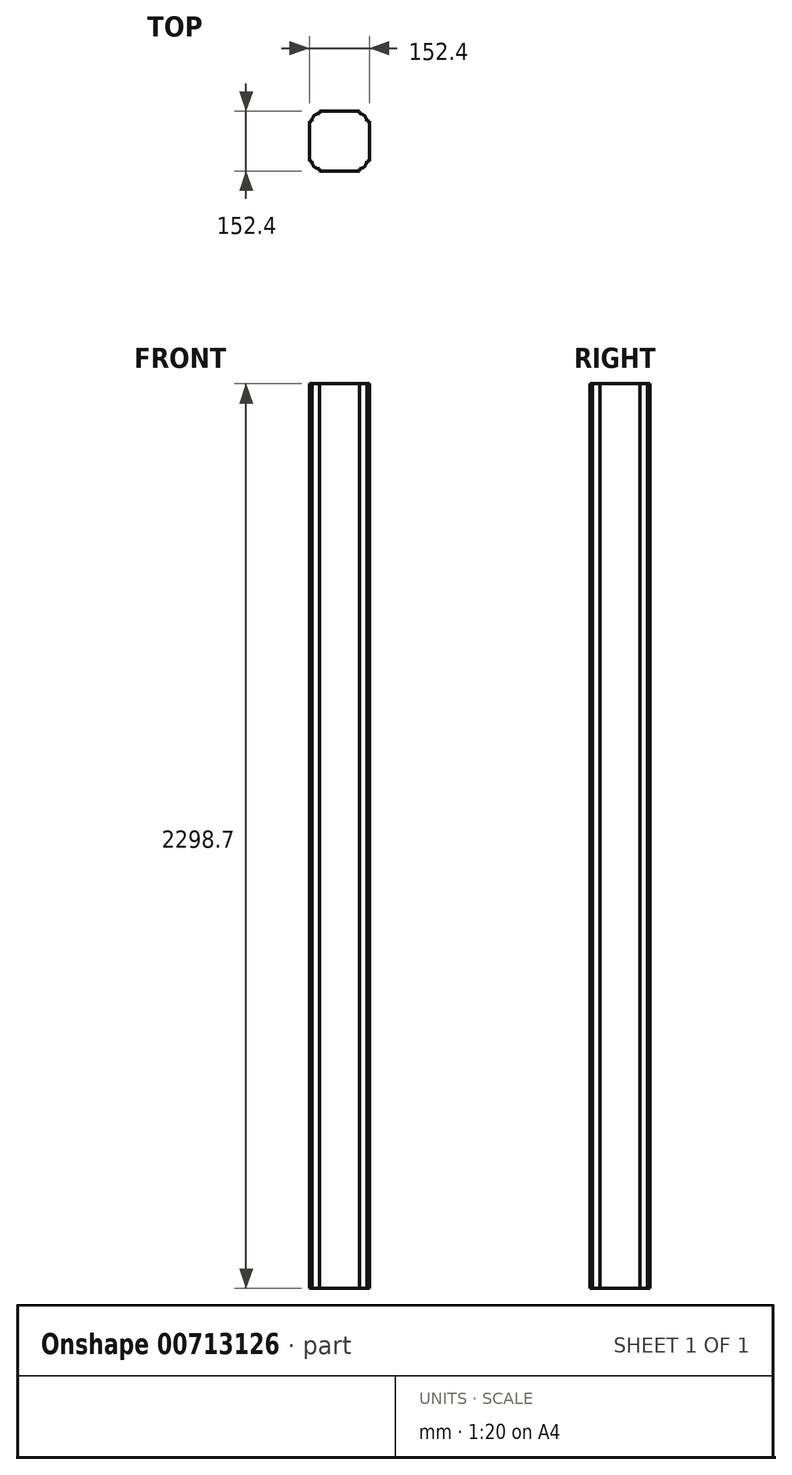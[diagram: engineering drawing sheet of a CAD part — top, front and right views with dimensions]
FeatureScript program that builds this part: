
annotation { "Feature Type Name" : "Feature", "Feature Type Description" : "" }
export const myFeature = defineFeature(function(context is Context, id is Id, definition is map)
    precondition{}
    {
        {
            var Q0;
            Q0=qCreatedBy(makeId("Top.planeOp"),FACE);
            var sketch = newSketch(context, id + "F0", { "sketchPlane" : qUnion([Q0])});
            skLineSegment(sketch, "E0.bottom", {"start": v(50.8, 0) * mm, "end": v(-50.8, 0) * mm});
            skLineSegment(sketch, "E0.top", {"start": v(50.8, 152.4) * mm, "end": v(-50.8, 152.4) * mm});
            skLineSegment(sketch, "E0.left", {"start": v(76.2, 25.4) * mm, "end": v(76.2, 127) * mm});
            skLineSegment(sketch, "E0.right", {"start": v(-76.2, 25.4) * mm, "end": v(-76.2, 127) * mm});
            skPoint(sketch, "E0.middle", {"position": v(0, 76.2) * mm});
            skLineSegment(sketch, "E1", {"start": v(-50.8, 152.4) * mm, "end": v(-50.8, 146.05) * mm});
            skLineSegment(sketch, "E2", {"start": v(-76.2, 152.4) * mm, "end": v(76.2, 0) * mm, "construction": true});
            skLineSegment(sketch, "E3", {"start": v(76.2, 152.4) * mm, "end": v(-76.2, 0) * mm, "construction": true});
            skLineSegment(sketch, "E4", {"start": v(0, 152.4) * mm, "end": v(0, 0) * mm, "construction": true});
            skLineSegment(sketch, "E5", {"start": v(-76.2, 76.2) * mm, "end": v(76.2, 76.2) * mm, "construction": true});
            skLineSegment(sketch, "E6.MirrorCS", {"start": v(-76.2, 127) * mm, "end": v(-69.85, 127) * mm});
            skArc(sketch, "E7", {"start": v(-50.8, 146.05) * mm, "mid": v(-64.27, 140.47) * mm, "end": v(-69.85, 127) * mm});
            skLineSegment(sketch, "E8.MirrorCS", {"start": v(50.8, 152.4) * mm, "end": v(50.8, 146.05) * mm});
            skLineSegment(sketch, "E9.MirrorCS", {"start": v(76.2, 127) * mm, "end": v(69.85, 127) * mm});
            skArc(sketch, "E10.MirrorCS", {"start": v(50.8, 146.05) * mm, "mid": v(64.27, 140.47) * mm, "end": v(69.85, 127) * mm});
            skLineSegment(sketch, "E11.MirrorCS", {"start": v(-50.8, 152.4) * mm, "end": v(50.8, 152.4) * mm});
            skLineSegment(sketch, "E12.MirrorCS", {"start": v(-76.2, 25.4) * mm, "end": v(-69.85, 25.4) * mm});
            skLineSegment(sketch, "E13.MirrorCS", {"start": v(50.8, 0) * mm, "end": v(50.8, 6.35) * mm});
            skLineSegment(sketch, "E14.MirrorCS", {"start": v(-50.8, 0) * mm, "end": v(-50.8, 6.35) * mm});
            skLineSegment(sketch, "E15.MirrorCS", {"start": v(76.2, 25.4) * mm, "end": v(69.85, 25.4) * mm});
            skArc(sketch, "E16.MirrorCS", {"start": v(-50.8, 6.35) * mm, "mid": v(-64.27, 11.93) * mm, "end": v(-69.85, 25.4) * mm});
            skArc(sketch, "E17.MirrorCS", {"start": v(50.8, 6.35) * mm, "mid": v(64.27, 11.93) * mm, "end": v(69.85, 25.4) * mm});
            skLineSegment(sketch, "E18.MirrorCS", {"start": v(-50.8, 0) * mm, "end": v(50.8, 0) * mm});
            skPoint(sketch, "E19.orphan", {"position": v(-76.2, 0) * mm});
            skPoint(sketch, "E20.orphan", {"position": v(76.2, 0) * mm});
            skPoint(sketch, "E21.orphan", {"position": v(-76.2, 152.4) * mm});
            skSolve(sketch);
        }
        {
            var Q0;
            Q0=makeQuery(id+"F0.imprint","IMPRINT",FACE,{"disambiguationData":[TD([[makeQuery(id+"F0.imprint","IMPRINT",EDGE,{"derivedFrom":sQuery(id+"F0.wireOp",EDGE,"E0.left")}),1.0]])]});
            extrude(context, id + "F1", {"entities" : qUnion([Q0]), "depth" : 2298.7 * mm, "offsetDistance" : 25.4 * mm});
        }
    });
